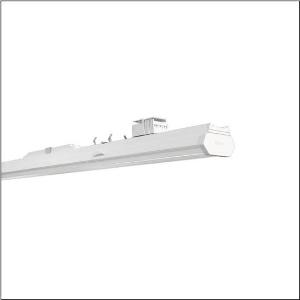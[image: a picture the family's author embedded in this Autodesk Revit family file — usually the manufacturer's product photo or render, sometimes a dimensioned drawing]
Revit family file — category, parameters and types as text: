
# Revit family: licross_r__11_protected_ho_51tp11cn4exs_0205
name_source: partatom
category: Lighting Fixtures
units: mm (PartAtom-declared; Revit-internal decimal feet)

## family parameters
Cut with Voids When Loaded = No
Host = Face
Light Source = No
Part Type = Normal
Room Calculation Point = No
Round Connector Dimension = Use Diameter
Shared = No

## types (1)
- --- (1 x LED, 14460 lm, 77.6 W, 4000K)
    Apparent Load = 78 VA
    CIE Flux Codes = 84 94 98 99 100
    Color Rendering = 80
    Color Temperature = 4000K
    Default Elevation = 1800 mm
    Description = Licross® 11 Protected HO, luminaire insert, of sheet steel, galvanised, coil coated, white, length: 1.500mm, width: 90mm, height: 101mm, LED rated luminous flux: 14.460lm, light colour: 840, control gear: ON/OFF Multilumen, CLOi, with plug, 3-pole, with phase selection, mains connection: 220..240V, AC, 50/60Hz, start of lifetime: 78W, end of service life: 87W, halogen-free wiring, primary light control with lens, of plastic, primary optical cover: cover, of PMMA, light emission: direct distribution, primary light characteristic: symmetric, protection rating (complete): IP64, insulation class (complete): insulation class I (protective earthing), certification: CE, ENEC, VDE, UKCA, protection symbol: D if used in an environment with conductive dust loads with corresponding accessories, impact resistance: IK06, permissible ambient temperature for indoor applications: -35..+35°C, corresponds to IFS (International Featured Standards) requirements for safety and quality in the food industry, reducing of maximum allowable ambient temperature of 5°C with ceiling mounting, LABS conformity tested according to VDMA 24364:2018-05, packaging unit: 1 piece
    Height = 92 mm
    Lamp = 1 x LED
    Lamp Light Flux = 14460 lm
    Lamp Power = 77.6 W
    Lamp count = 1
    Length = 1500 mm
    Luminous efficacy = 186 lm/W
    Manufacturer = Siteco
    ModVariant = No
    Model = 51TP11CN4EXS
    Mounting Place = Ceiling
    Mounting Type = Pendant
    Number of Poles = 1
    OnlyDefault = Yes
    Power Factor = 1
    Product Name = Licross® 11 Protected HO
    Product group = luminaire insert
    ProductGroupID = 901
    Protection Class = Protection class I
    Protection Degree = IP 64
    RLX_Detail_Level = 1
    RLX_Emergency_Light_Flux = 0 lm
    RLX_Emergency_Type = 0
    RLX_Emergency_Type_DB = No
    RlxData = <blob elided: 22089 chars, md5=ec5cc6ec>
    Socket = socket
    Standby Power = 0 W
    System Light Flux = 14460 lm
    System Power = 78 W
    Type Comments = factory setting: luminous flux: 100 % | (A | C | E) | 181 mA
    Type Image = l_1256148.jpg
    URL = http://relux.com
    VarID = @adj_055171
    Voltage = 0 V
    Weight = 0.00 kg
    Width = 88 mm

## geometry (parser evidence)
native form markers: Blend x4, Sweep x11
no freeform markers — native parametric forms only
